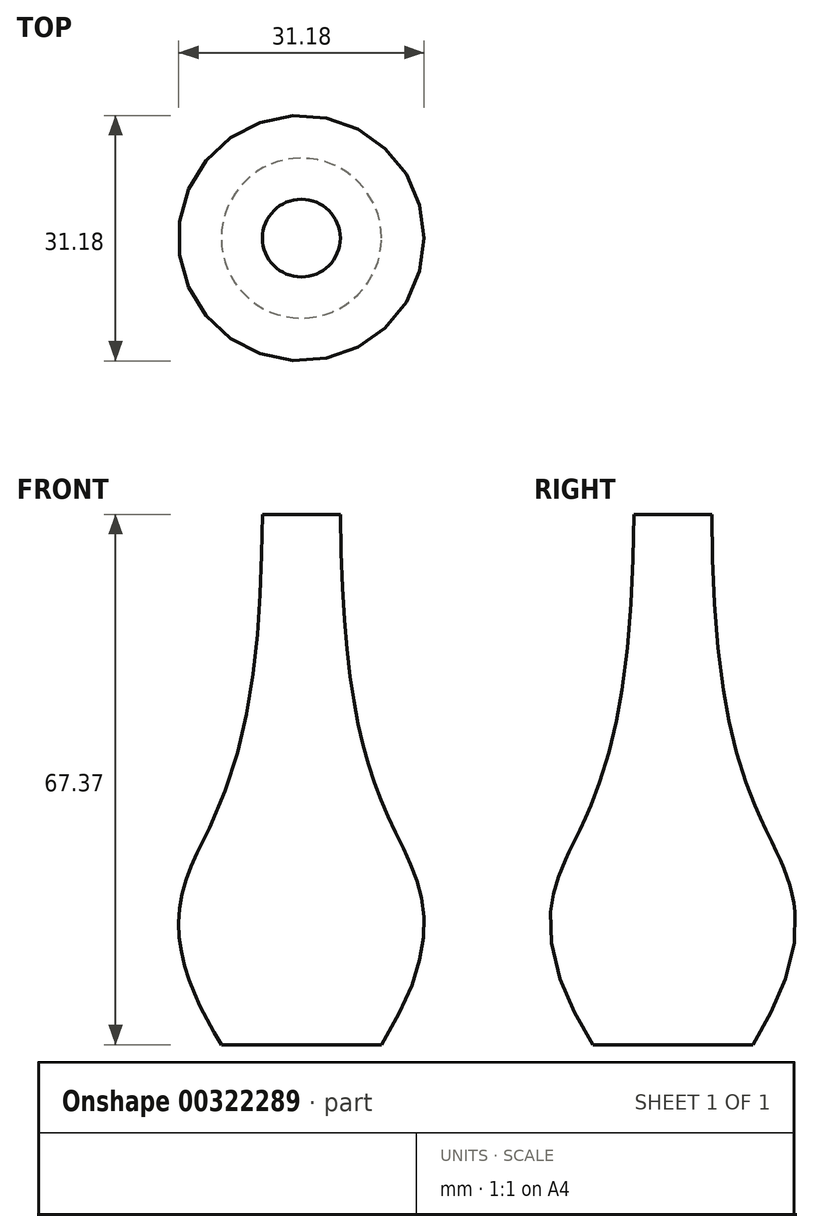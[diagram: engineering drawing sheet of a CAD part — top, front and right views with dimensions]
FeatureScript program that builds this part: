
annotation { "Feature Type Name" : "Feature", "Feature Type Description" : "" }
export const myFeature = defineFeature(function(context is Context, id is Id, definition is map)
    precondition{}
    {
        {
            var Q0;
            Q0=qCreatedBy(makeId("Front.planeOp"),FACE);
            var sketch = newSketch(context, id + "F0", { "sketchPlane" : qUnion([Q0])});
            skFitSpline(sketch, "E0", {"points": [v(-10.16, 0) * mm, v(-11.53, 27.87) * mm, v(-4.94, 67.37) * mm], "startDerivative": vector(-60.24, 97.05) * mm, "endDerivative": vector(0.96, 116.55) * mm});
            skFitSpline(sketch, "E1.MirrorCS", {"points": [v(10.16, 0) * mm, v(11.53, 27.87) * mm, v(4.94, 67.37) * mm], "startDerivative": vector(60.24, 97.05) * mm, "endDerivative": vector(-0.96, 116.55) * mm});
            skLineSegment(sketch, "E2", {"start": v(-10.16, 0) * mm, "end": v(10.16, 0) * mm});
            skLineSegment(sketch, "E3", {"start": v(-4.94, 67.37) * mm, "end": v(4.94, 67.37) * mm});
            skLineSegment(sketch, "E4", {"start": v(0, 67.37) * mm, "end": v(0, 0) * mm});
            skSolve(sketch);
        }
        {
            var Q0;
            {var subQ0=sQuery(id+"F0.wireOp",EDGE,"E1.MirrorCS");Q0=makeQuery(id+"F0.imprint","IMPRINT",FACE,{"disambiguationData":[TD([[makeQuery(id+"F0.imprint","IMPRINT",EDGE,{"derivedFrom":subQ0}),1.0]])]});}
            var Q1;
            Q1=sQuery(id+"F0.wireOp",EDGE,"E4");
            revolve(context, id + "F1", {"entities" : qUnion([Q0]), "axis" : qUnion([Q1]), "revolveType" : RevolveType.FULL});
        }
    });
